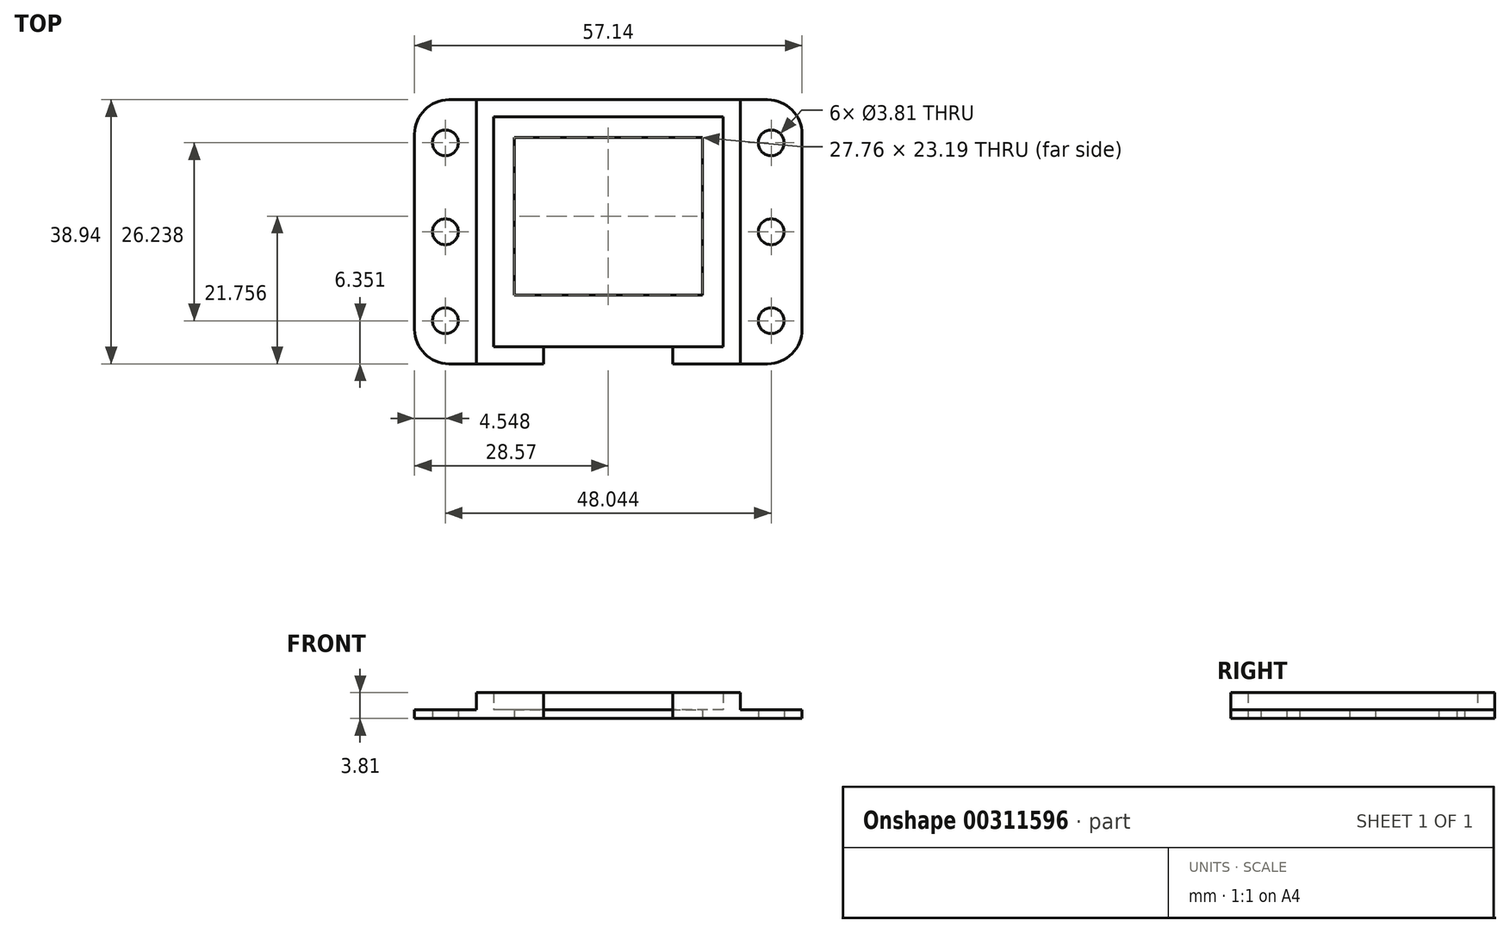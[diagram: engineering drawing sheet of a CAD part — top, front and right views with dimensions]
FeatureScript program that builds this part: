
annotation { "Feature Type Name" : "Feature", "Feature Type Description" : "" }
export const myFeature = defineFeature(function(context is Context, id is Id, definition is map)
    precondition{}
    {
        {
            var Q0;
            Q0=qCreatedBy(makeId("Top.planeOp"),FACE);
            var sketch = newSketch(context, id + "F0", { "sketchPlane" : qUnion([Q0])});
            skPoint(sketch, "E0.middle", {"position": v(0, 0) * mm});
            skLineSegment(sketch, "E1.bottom", {"start": v(16.93, 16.93) * mm, "end": v(-16.93, 16.93) * mm});
            skLineSegment(sketch, "E1.top", {"start": v(16.93, -16.93) * mm, "end": v(-16.93, -16.93) * mm});
            skLineSegment(sketch, "E1.left", {"start": v(16.93, 16.93) * mm, "end": v(16.93, -16.93) * mm});
            skLineSegment(sketch, "E1.right", {"start": v(-16.93, 16.93) * mm, "end": v(-16.93, -16.93) * mm});
            skLineSegment(sketch, "E2.bottom", {"start": v(19.47, 19.47) * mm, "end": v(-19.47, 19.47) * mm});
            skLineSegment(sketch, "E2.top", {"start": v(19.47, -19.47) * mm, "end": v(-19.47, -19.47) * mm});
            skLineSegment(sketch, "E2.left", {"start": v(19.47, 19.47) * mm, "end": v(19.47, -19.47) * mm});
            skLineSegment(sketch, "E2.right", {"start": v(-19.47, 19.47) * mm, "end": v(-19.47, -19.47) * mm});
            skLineSegment(sketch, "E3.bottom", {"start": v(28.58, 19.47) * mm, "end": v(-28.58, 19.47) * mm});
            skLineSegment(sketch, "E3.top", {"start": v(28.58, -19.47) * mm, "end": v(-28.58, -19.47) * mm});
            skLineSegment(sketch, "E3.left", {"start": v(28.58, 19.47) * mm, "end": v(28.58, -19.47) * mm});
            skLineSegment(sketch, "E3.right", {"start": v(-28.58, 19.47) * mm, "end": v(-28.58, -19.47) * mm});
            skCircle(sketch, "E4", {"center": v(24.02, 0) * mm, "radius": 1.9 * mm});
            skCircle(sketch, "E5.MirrorC", {"center": v(-24.02, 0) * mm, "radius": 1.9 * mm});
            skLineSegment(sketch, "E6.bottom", {"start": v(-13.88, 13.88) * mm, "end": v(13.88, 13.88) * mm});
            skLineSegment(sketch, "E6.top", {"start": v(-13.88, -9.3) * mm, "end": v(13.88, -9.3) * mm});
            skLineSegment(sketch, "E6.left", {"start": v(-13.88, 13.88) * mm, "end": v(-13.88, -9.3) * mm});
            skLineSegment(sketch, "E6.right", {"start": v(13.88, 13.88) * mm, "end": v(13.88, -9.3) * mm});
            skLineSegment(sketch, "E7.bottom", {"start": v(-9.53, -19.47) * mm, "end": v(9.53, -19.47) * mm});
            skLineSegment(sketch, "E7.top", {"start": v(-9.53, -16.93) * mm, "end": v(9.53, -16.93) * mm});
            skLineSegment(sketch, "E7.left", {"start": v(-9.53, -19.47) * mm, "end": v(-9.53, -16.93) * mm});
            skLineSegment(sketch, "E7.right", {"start": v(9.53, -19.47) * mm, "end": v(9.53, -16.93) * mm});
            skLineSegment(sketch, "E8", {"start": v(0, -19.47) * mm, "end": v(0, -16.93) * mm, "construction": true});
            skLineSegment(sketch, "E9", {"start": v(19.47, -19.47) * mm, "end": v(28.58, -19.47) * mm});
            skLineSegment(sketch, "E10", {"start": v(24.02, -19.47) * mm, "end": v(24.02, 19.47) * mm, "construction": true});
            skCircle(sketch, "E11", {"center": v(24.02, -13.12) * mm, "radius": 1.9 * mm});
            skCircle(sketch, "E12", {"center": v(24.02, 13.12) * mm, "radius": 1.9 * mm});
            skCircle(sketch, "E13.MirrorC", {"center": v(-24.02, -13.12) * mm, "radius": 1.9 * mm});
            skCircle(sketch, "E14.MirrorC", {"center": v(-24.02, 13.12) * mm, "radius": 1.9 * mm});
            skSolve(sketch);
        }
        {
            var Q0;
            Q0=makeQuery(id+"F0.imprint","IMPRINT",FACE,{"disambiguationData":[TD([[makeQuery(id+"F0.imprint","IMPRINT",EDGE,{"derivedFrom":sQuery(id+"F0.wireOp",EDGE,"E1.bottom")}),1.0]])]});
            extrude(context, id + "F1", {"entities" : qUnion([Q0]), "depth" : 1.27 * mm, "offsetDistance" : 25.4 * mm});
        }
        {
            var Q0;
            Q0=makeQuery(id+"F0.imprint","IMPRINT",FACE,{"disambiguationData":[TD([[makeQuery(id+"F0.imprint","IMPRINT",EDGE,{"derivedFrom":sQuery(id+"F0.wireOp",EDGE,"E1.bottom")}),-1.0]])]});
            extrude(context, id + "F2", {"entities" : qUnion([Q0]), "operationType" : NewBodyOperationType.ADD, "depth" : 3.8 * mm, "offsetDistance" : 25.4 * mm});
        }
        {
            var Q0;
            {var subQ1=sQuery(id+"F0.wireOp",EDGE,"E2.right");Q0=makeQuery(id+"F0.imprint","IMPRINT",FACE,{"disambiguationData":[TD([[makeQuery(id+"F0.imprint","IMPRINT",EDGE,{"derivedFrom":subQ1}),-1.0]])]});}
            var Q1;
            {var subQ2=sQuery(id+"F0.wireOp",EDGE,"E2.left");Q1=makeQuery(id+"F0.imprint","IMPRINT",FACE,{"disambiguationData":[TD([[makeQuery(id+"F0.imprint","IMPRINT",EDGE,{"derivedFrom":subQ2}),1.0]])]});}
            var Q2;
            Q2=makeQuery(id+"F0.imprint","IMPRINT",FACE,{"disambiguationData":[TD([[makeQuery(id+"F0.imprint","IMPRINT",EDGE,{"derivedFrom":sQuery(id+"F0.wireOp",EDGE,"E1.bottom")}),-1.0]])]});
            var Q3;
            Q3=makeQuery(id+"F0.imprint","IMPRINT",FACE,{"disambiguationData":[TD([[makeQuery(id+"F0.imprint","IMPRINT",EDGE,{"derivedFrom":sQuery(id+"F0.wireOp",EDGE,"E1.bottom")}),1.0]])]});
            extrude(context, id + "F3", {"entities" : qUnion([Q0, Q1, Q2, Q3]), "operationType" : NewBodyOperationType.ADD, "depth" : 1.27 * mm, "offsetDistance" : 25.4 * mm});
        }
        {
            var Q0;
            Q0=makeQuery(id+"F3.opExtrude","SWEPT_EDGE",EDGE,{"disambiguationData":[OSD([sQuery(id+"F0.wireOp",EDGE,"E3.bottom"),sQuery(id+"F0.wireOp",EDGE,"E3.right")])]});
            var Q1;
            Q1=makeQuery(id+"F3.opExtrude","SWEPT_EDGE",EDGE,{"disambiguationData":[OSD([sQuery(id+"F0.wireOp",EDGE,"E3.top"),sQuery(id+"F0.wireOp",EDGE,"E3.right")])]});
            var Q2;
            Q2=makeQuery(id+"F3.opExtrude","SWEPT_EDGE",EDGE,{"disambiguationData":[OSD([sQuery(id+"F0.wireOp",EDGE,"E3.bottom"),sQuery(id+"F0.wireOp",EDGE,"E3.left")])]});
            var Q3;
            Q3=makeQuery(id+"F3.opExtrude","SWEPT_EDGE",EDGE,{"disambiguationData":[OSD([sQuery(id+"F0.wireOp",EDGE,"E3.left"),sQuery(id+"F0.wireOp",EDGE,"E9")])]});
            fillet(context, id + "F4", {"entities" : qUnion([Q0, Q1, Q2, Q3]), "radius" : 5.08 * mm, "tangentPropagation" : true, "allowEdgeOverflow" : false});
        }
    });
